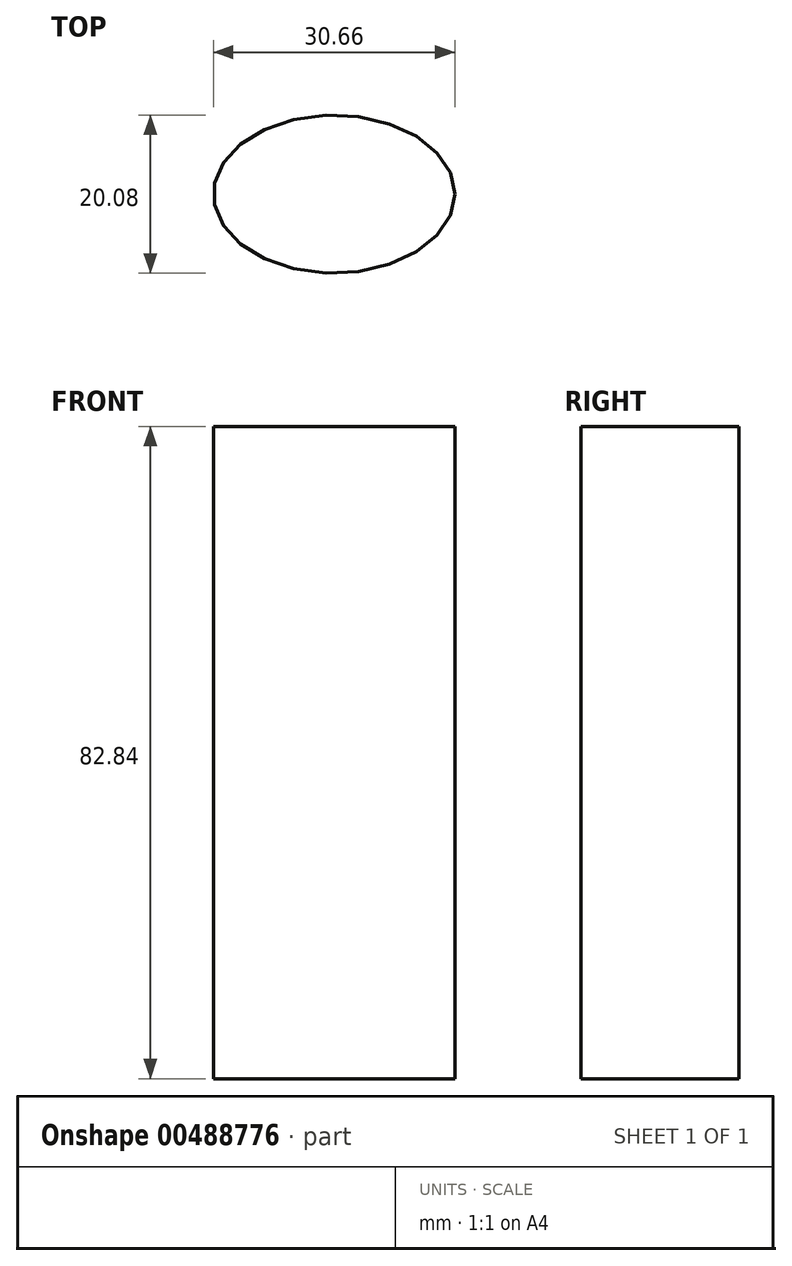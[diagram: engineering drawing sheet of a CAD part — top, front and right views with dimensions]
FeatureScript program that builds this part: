
annotation { "Feature Type Name" : "Feature", "Feature Type Description" : "" }
export const myFeature = defineFeature(function(context is Context, id is Id, definition is map)
    precondition{}
    {
        {
            var Q0;
            Q0=qCreatedBy(makeId("Top.planeOp"),FACE);
            var sketch = newSketch(context, id + "F0", { "sketchPlane" : qUnion([Q0])});
            skEllipse(sketch, "E0", {"center": v(0, 0) * mm, "majorRadius": 15.33 * mm, "minorRadius": 10.04 * mm, "majorAxis": v(1, 0)});
            skSolve(sketch);
        }
        {
            var Q0;
            Q0 = qSketchRegion(id + "F0", true);
            extrude(context, id + "F1", {"entities" : qUnion([Q0]), "depth" : 82.84 * mm});
        }
    });
